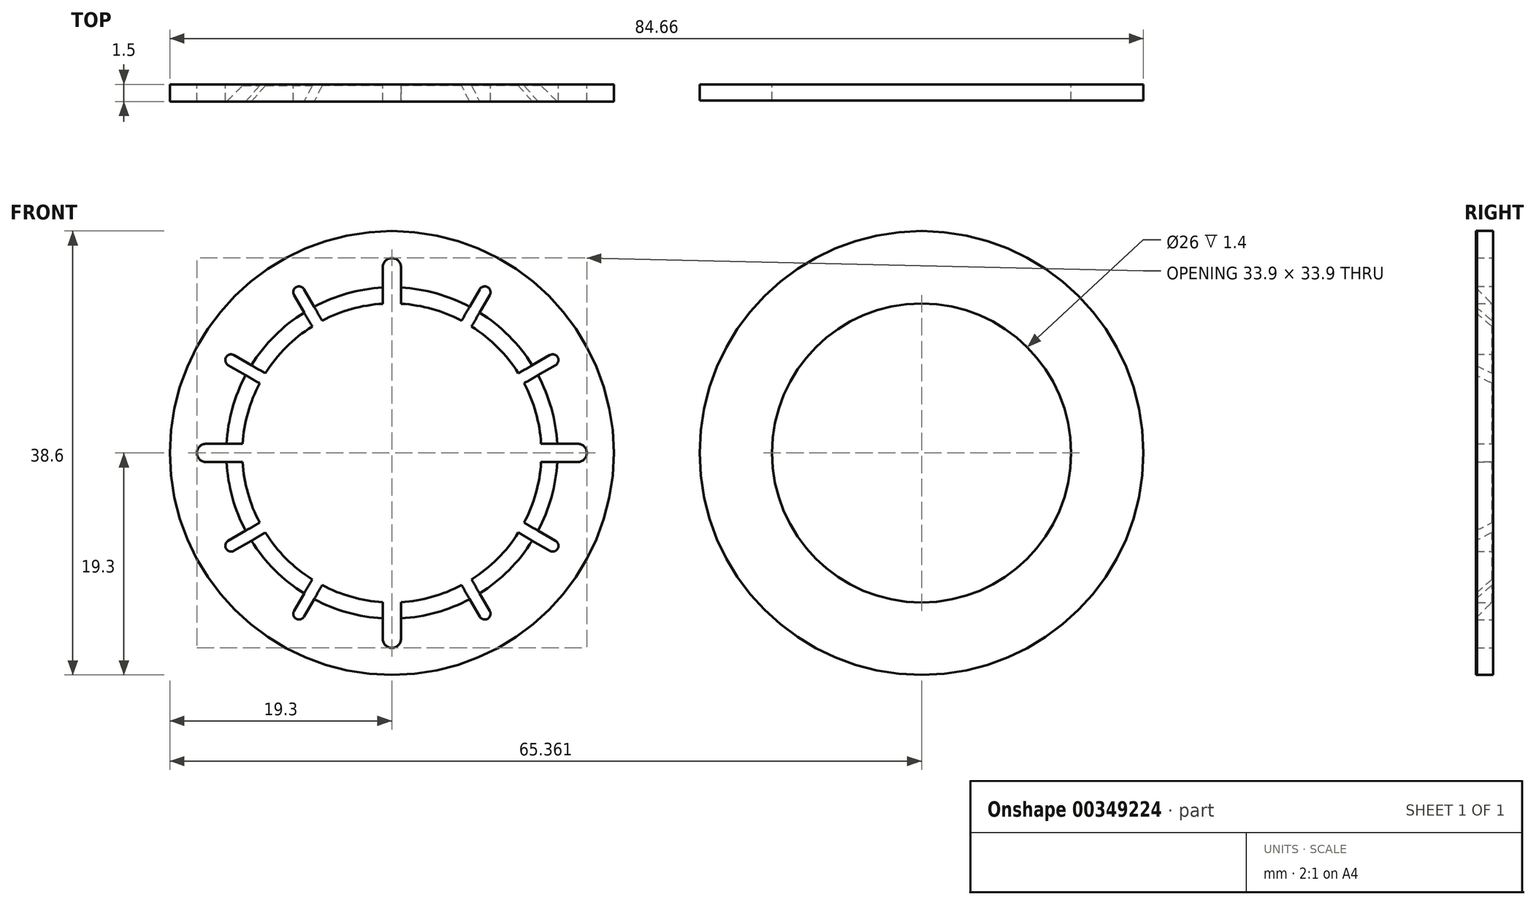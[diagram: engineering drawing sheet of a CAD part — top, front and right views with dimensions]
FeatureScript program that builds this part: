
annotation { "Feature Type Name" : "Feature", "Feature Type Description" : "" }
export const myFeature = defineFeature(function(context is Context, id is Id, definition is map)
    precondition{}
    {
        {
            var Q0;
            Q0=qCreatedBy(makeId("Front.planeOp"),FACE);
            var sketch = newSketch(context, id + "F0", { "sketchPlane" : qUnion([Q0])});
            skCircle(sketch, "E0", {"center": v(0, 0) * mm, "radius": 19.3 * mm});
            skCircle(sketch, "E1", {"center": v(0, 0) * mm, "radius": 13 * mm});
            skLineSegment(sketch, "E2", {"start": v(0, 0) * mm, "end": v(-19.3, 0) * mm});
            skLineSegment(sketch, "E3", {"start": v(0, 0) * mm, "end": v(0, 19.3) * mm});
            skLineSegment(sketch, "E4", {"start": v(-19.3, 0) * mm, "end": v(-13, 0) * mm});
            skCircle(sketch, "E5", {"center": v(-16.15, 0) * mm, "radius": 0.5 * mm});
            skLineSegment(sketch, "E6", {"start": v(-16.15, 0.5) * mm, "end": v(-13, 0.5) * mm});
            skLineSegment(sketch, "E7.MirrorCS", {"start": v(-16.15, -0.5) * mm, "end": v(-13, -0.5) * mm});
            skCircle(sketch, "E8.1.0", {"center": v(-13.99, -8.07) * mm, "radius": 0.5 * mm});
            skLineSegment(sketch, "E8.1.1", {"start": v(-13.74, -8.5) * mm, "end": v(-11, -6.93) * mm});
            skLineSegment(sketch, "E8.1.2", {"start": v(-14.24, -7.64) * mm, "end": v(-11.5, -6.06) * mm});
            skCircle(sketch, "E8.2.0", {"center": v(-8.08, -13.99) * mm, "radius": 0.5 * mm});
            skLineSegment(sketch, "E8.2.1", {"start": v(-7.64, -14.24) * mm, "end": v(-6.06, -11.5) * mm});
            skLineSegment(sketch, "E8.2.2", {"start": v(-8.5, -13.74) * mm, "end": v(-6.93, -11) * mm});
            skCircle(sketch, "E9.1.3.0", {"center": v(0, -16.15) * mm, "radius": 0.5 * mm});
            skLineSegment(sketch, "E9.2.3.0", {"start": v(0.5, -16.15) * mm, "end": v(0.5, -13) * mm});
            skLineSegment(sketch, "E9.5.3.0", {"start": v(-0.5, -16.15) * mm, "end": v(-0.5, -13) * mm});
            skCircle(sketch, "E9.1.4.0", {"center": v(8.07, -13.99) * mm, "radius": 0.5 * mm});
            skLineSegment(sketch, "E9.2.4.0", {"start": v(8.5, -13.74) * mm, "end": v(6.93, -11) * mm});
            skLineSegment(sketch, "E9.5.4.0", {"start": v(7.64, -14.24) * mm, "end": v(6.06, -11.5) * mm});
            skCircle(sketch, "E9.1.5.0", {"center": v(13.99, -8.07) * mm, "radius": 0.5 * mm});
            skLineSegment(sketch, "E9.2.5.0", {"start": v(14.24, -7.64) * mm, "end": v(11.5, -6.06) * mm});
            skLineSegment(sketch, "E9.5.5.0", {"start": v(13.74, -8.5) * mm, "end": v(11, -6.93) * mm});
            skCircle(sketch, "E9.1.6.0", {"center": v(16.15, 0) * mm, "radius": 0.5 * mm});
            skLineSegment(sketch, "E9.2.6.0", {"start": v(16.15, 0.5) * mm, "end": v(13, 0.5) * mm});
            skLineSegment(sketch, "E9.5.6.0", {"start": v(16.15, -0.5) * mm, "end": v(13, -0.5) * mm});
            skCircle(sketch, "E9.1.7.0", {"center": v(13.99, 8.07) * mm, "radius": 0.5 * mm});
            skLineSegment(sketch, "E9.2.7.0", {"start": v(13.74, 8.5) * mm, "end": v(11, 6.93) * mm});
            skLineSegment(sketch, "E9.5.7.0", {"start": v(14.24, 7.64) * mm, "end": v(11.5, 6.06) * mm});
            skCircle(sketch, "E9.1.8.0", {"center": v(8.08, 13.99) * mm, "radius": 0.5 * mm});
            skLineSegment(sketch, "E9.2.8.0", {"start": v(7.64, 14.24) * mm, "end": v(6.06, 11.5) * mm});
            skLineSegment(sketch, "E9.5.8.0", {"start": v(8.5, 13.74) * mm, "end": v(6.93, 11) * mm});
            skCircle(sketch, "E9.1.9.0", {"center": v(0, 16.15) * mm, "radius": 0.5 * mm});
            skLineSegment(sketch, "E9.2.9.0", {"start": v(-0.5, 16.15) * mm, "end": v(-0.5, 13) * mm});
            skLineSegment(sketch, "E9.5.9.0", {"start": v(0.5, 16.15) * mm, "end": v(0.5, 13) * mm});
            skCircle(sketch, "E9.1.10.0", {"center": v(-8.08, 13.99) * mm, "radius": 0.5 * mm});
            skLineSegment(sketch, "E9.2.10.0", {"start": v(-8.5, 13.74) * mm, "end": v(-6.93, 11) * mm});
            skLineSegment(sketch, "E9.5.10.0", {"start": v(-7.64, 14.24) * mm, "end": v(-6.06, 11.5) * mm});
            skCircle(sketch, "E9.1.11.0", {"center": v(-13.99, 8.08) * mm, "radius": 0.5 * mm});
            skLineSegment(sketch, "E9.2.11.0", {"start": v(-14.24, 7.64) * mm, "end": v(-11.5, 6.06) * mm});
            skLineSegment(sketch, "E9.5.11.0", {"start": v(-13.74, 8.5) * mm, "end": v(-11, 6.93) * mm});
            skCircle(sketch, "E10", {"center": v(-16.15, 0) * mm, "radius": 0.8 * mm});
            skLineSegment(sketch, "E11", {"start": v(-16.15, 0.8) * mm, "end": v(-12.98, 0.8) * mm});
            skLineSegment(sketch, "E12.MirrorCS", {"start": v(-16.15, -0.8) * mm, "end": v(-12.98, -0.8) * mm});
            skCircle(sketch, "E13.1.0", {"center": v(0, -16.15) * mm, "radius": 0.8 * mm});
            skLineSegment(sketch, "E13.1.1", {"start": v(-0.8, -16.15) * mm, "end": v(-0.8, -12.98) * mm});
            skLineSegment(sketch, "E13.1.2", {"start": v(0.8, -16.15) * mm, "end": v(0.8, -12.98) * mm});
            skCircle(sketch, "E13.2.0", {"center": v(16.15, 0) * mm, "radius": 0.8 * mm});
            skLineSegment(sketch, "E13.2.1", {"start": v(16.15, -0.8) * mm, "end": v(12.98, -0.8) * mm});
            skLineSegment(sketch, "E13.2.2", {"start": v(16.15, 0.8) * mm, "end": v(12.98, 0.8) * mm});
            skCircle(sketch, "E14.1.3.0", {"center": v(0, 16.15) * mm, "radius": 0.8 * mm});
            skLineSegment(sketch, "E14.2.3.0", {"start": v(0.8, 16.15) * mm, "end": v(0.8, 12.98) * mm});
            skLineSegment(sketch, "E14.5.3.0", {"start": v(-0.8, 16.15) * mm, "end": v(-0.8, 12.98) * mm});
            skCircle(sketch, "E15", {"center": v(46.06, 0) * mm, "radius": 19.3 * mm});
            skCircle(sketch, "E16", {"center": v(46.06, 0) * mm, "radius": 13 * mm});
            skSolve(sketch);
        }
        {
            var Q0;
            {var subQ11=sQuery(id+"F0.wireOp",EDGE,"E9.2.10.0");Q0=makeQuery(id+"F0.imprint","IMPRINT",FACE,{"disambiguationData":[TD([[makeQuery(id+"F0.imprint","IMPRINT",EDGE,{"derivedFrom":subQ11}),-1.0]])]});}
            var Q1;
            {var subQ6=sQuery(id+"F0.wireOp",EDGE,"E8.1.1");Q1=makeQuery(id+"F0.imprint","IMPRINT",FACE,{"disambiguationData":[TD([[makeQuery(id+"F0.imprint","IMPRINT",EDGE,{"derivedFrom":subQ6}),-1.0]])]});}
            extrude(context, id + "F1", {"entities" : qUnion([Q0, Q1]), "depth" : 1.5 * mm});
        }
        {
            var Q0;
            {var subQ0=sQuery(id+"F0.wireOp",EDGE,"E1");Q0=makeQuery(id+"F1.opExtrude","CAP_EDGE",EDGE,{"disambiguationData":[OSD([subQ0]),TDD([makeQuery(id+"F0.imprint","IMPRINT",EDGE,{"disambiguationData":[TD([[makeQuery(id+"F0.imprint","INTERSECT",VERTEX,{"derivedFrom":[subQ0,sQuery(id+"F0.wireOp",EDGE,"E9.2.11.0")]}),-1.0]])],"derivedFrom":subQ0})])],"isStart":false});}
            var Q1;
            {var subQ0=sQuery(id+"F0.wireOp",EDGE,"E1");Q1=makeQuery(id+"F1.opExtrude","CAP_EDGE",EDGE,{"disambiguationData":[OSD([subQ0]),TDD([makeQuery(id+"F0.imprint","IMPRINT",EDGE,{"disambiguationData":[TD([[makeQuery(id+"F0.imprint","INTERSECT",VERTEX,{"derivedFrom":[subQ0,sQuery(id+"F0.wireOp",EDGE,"E9.2.10.0")]}),-1.0]])],"derivedFrom":subQ0})])],"isStart":false});}
            var Q2;
            {var subQ0=sQuery(id+"F0.wireOp",EDGE,"E1");Q2=makeQuery(id+"F1.opExtrude","CAP_EDGE",EDGE,{"disambiguationData":[OSD([subQ0]),TDD([makeQuery(id+"F0.imprint","IMPRINT",EDGE,{"disambiguationData":[TD([[makeQuery(id+"F0.imprint","INTERSECT",VERTEX,{"derivedFrom":[subQ0,sQuery(id+"F0.wireOp",EDGE,"E9.5.10.0")]}),1.0]])],"derivedFrom":subQ0})])],"isStart":false});}
            var Q3;
            {var subQ0=sQuery(id+"F0.wireOp",EDGE,"E1");Q3=makeQuery(id+"F1.opExtrude","CAP_EDGE",EDGE,{"disambiguationData":[OSD([subQ0]),TDD([makeQuery(id+"F0.imprint","IMPRINT",EDGE,{"disambiguationData":[TD([[makeQuery(id+"F0.imprint","INTERSECT",VERTEX,{"derivedFrom":[subQ0,sQuery(id+"F0.wireOp",EDGE,"E9.2.8.0")]}),-1.0]])],"derivedFrom":subQ0})])],"isStart":false});}
            var Q4;
            {var subQ0=sQuery(id+"F0.wireOp",EDGE,"E1");Q4=makeQuery(id+"F1.opExtrude","CAP_EDGE",EDGE,{"disambiguationData":[OSD([subQ0]),TDD([makeQuery(id+"F0.imprint","IMPRINT",EDGE,{"disambiguationData":[TD([[makeQuery(id+"F0.imprint","INTERSECT",VERTEX,{"derivedFrom":[subQ0,sQuery(id+"F0.wireOp",EDGE,"E9.2.7.0")]}),-1.0]])],"derivedFrom":subQ0})])],"isStart":false});}
            var Q5;
            {var subQ0=sQuery(id+"F0.wireOp",EDGE,"E1");Q5=makeQuery(id+"F1.opExtrude","CAP_EDGE",EDGE,{"disambiguationData":[OSD([subQ0]),TDD([makeQuery(id+"F0.imprint","IMPRINT",EDGE,{"disambiguationData":[TD([[makeQuery(id+"F0.imprint","INTERSECT",VERTEX,{"derivedFrom":[subQ0,sQuery(id+"F0.wireOp",EDGE,"E9.5.7.0")]}),1.0]])],"derivedFrom":subQ0})])],"isStart":false});}
            var Q6;
            {var subQ0=sQuery(id+"F0.wireOp",EDGE,"E1");Q6=makeQuery(id+"F1.opExtrude","CAP_EDGE",EDGE,{"disambiguationData":[OSD([subQ0]),TDD([makeQuery(id+"F0.imprint","IMPRINT",EDGE,{"disambiguationData":[TD([[makeQuery(id+"F0.imprint","INTERSECT",VERTEX,{"derivedFrom":[subQ0,sQuery(id+"F0.wireOp",EDGE,"E9.2.5.0")]}),-1.0]])],"derivedFrom":subQ0})])],"isStart":false});}
            var Q7;
            {var subQ0=sQuery(id+"F0.wireOp",EDGE,"E1");Q7=makeQuery(id+"F1.opExtrude","CAP_EDGE",EDGE,{"disambiguationData":[OSD([subQ0]),TDD([makeQuery(id+"F0.imprint","IMPRINT",EDGE,{"disambiguationData":[TD([[makeQuery(id+"F0.imprint","INTERSECT",VERTEX,{"derivedFrom":[subQ0,sQuery(id+"F0.wireOp",EDGE,"E9.2.4.0")]}),-1.0]])],"derivedFrom":subQ0})])],"isStart":false});}
            var Q8;
            {var subQ0=sQuery(id+"F0.wireOp",EDGE,"E1");Q8=makeQuery(id+"F1.opExtrude","CAP_EDGE",EDGE,{"disambiguationData":[OSD([subQ0]),TDD([makeQuery(id+"F0.imprint","IMPRINT",EDGE,{"disambiguationData":[TD([[makeQuery(id+"F0.imprint","INTERSECT",VERTEX,{"derivedFrom":[subQ0,sQuery(id+"F0.wireOp",EDGE,"E9.5.4.0")]}),1.0]])],"derivedFrom":subQ0})])],"isStart":false});}
            var Q9;
            {var subQ0=sQuery(id+"F0.wireOp",EDGE,"E1");Q9=makeQuery(id+"F1.opExtrude","CAP_EDGE",EDGE,{"disambiguationData":[OSD([subQ0]),TDD([makeQuery(id+"F0.imprint","IMPRINT",EDGE,{"disambiguationData":[TD([[makeQuery(id+"F0.imprint","INTERSECT",VERTEX,{"derivedFrom":[subQ0,sQuery(id+"F0.wireOp",EDGE,"E8.2.1")]}),-1.0]])],"derivedFrom":subQ0})])],"isStart":false});}
            var Q10;
            {var subQ0=sQuery(id+"F0.wireOp",EDGE,"E1");Q10=makeQuery(id+"F1.opExtrude","CAP_EDGE",EDGE,{"disambiguationData":[OSD([subQ0]),TDD([makeQuery(id+"F0.imprint","IMPRINT",EDGE,{"disambiguationData":[TD([[makeQuery(id+"F0.imprint","INTERSECT",VERTEX,{"derivedFrom":[subQ0,sQuery(id+"F0.wireOp",EDGE,"E8.1.1")]}),-1.0]])],"derivedFrom":subQ0})])],"isStart":false});}
            var Q11;
            {var subQ0=sQuery(id+"F0.wireOp",EDGE,"E1");Q11=makeQuery(id+"F1.opExtrude","CAP_EDGE",EDGE,{"disambiguationData":[OSD([subQ0]),TDD([makeQuery(id+"F0.imprint","IMPRINT",EDGE,{"disambiguationData":[TD([[makeQuery(id+"F0.imprint","INTERSECT",VERTEX,{"derivedFrom":[subQ0,sQuery(id+"F0.wireOp",EDGE,"E8.1.2")]}),1.0]])],"derivedFrom":subQ0})])],"isStart":false});}
            chamfer(context, id + "F2", {"entities" : qUnion([Q0, Q1, Q2, Q3, Q4, Q5, Q6, Q7, Q8, Q9, Q10, Q11]), "width" : 1.4 * mm, "tangentPropagation" : true});
        }
        {
            var Q0;
            Q0=makeQuery(id+"F0.imprint","IMPRINT",FACE,{"disambiguationData":[TD([[makeQuery(id+"F0.imprint","IMPRINT",EDGE,{"derivedFrom":sQuery(id+"F0.wireOp",EDGE,"E15")}),1.0]])]});
            extrude(context, id + "F3", {"entities" : qUnion([Q0]), "depth" : 1.4 * mm});
        }
    });
